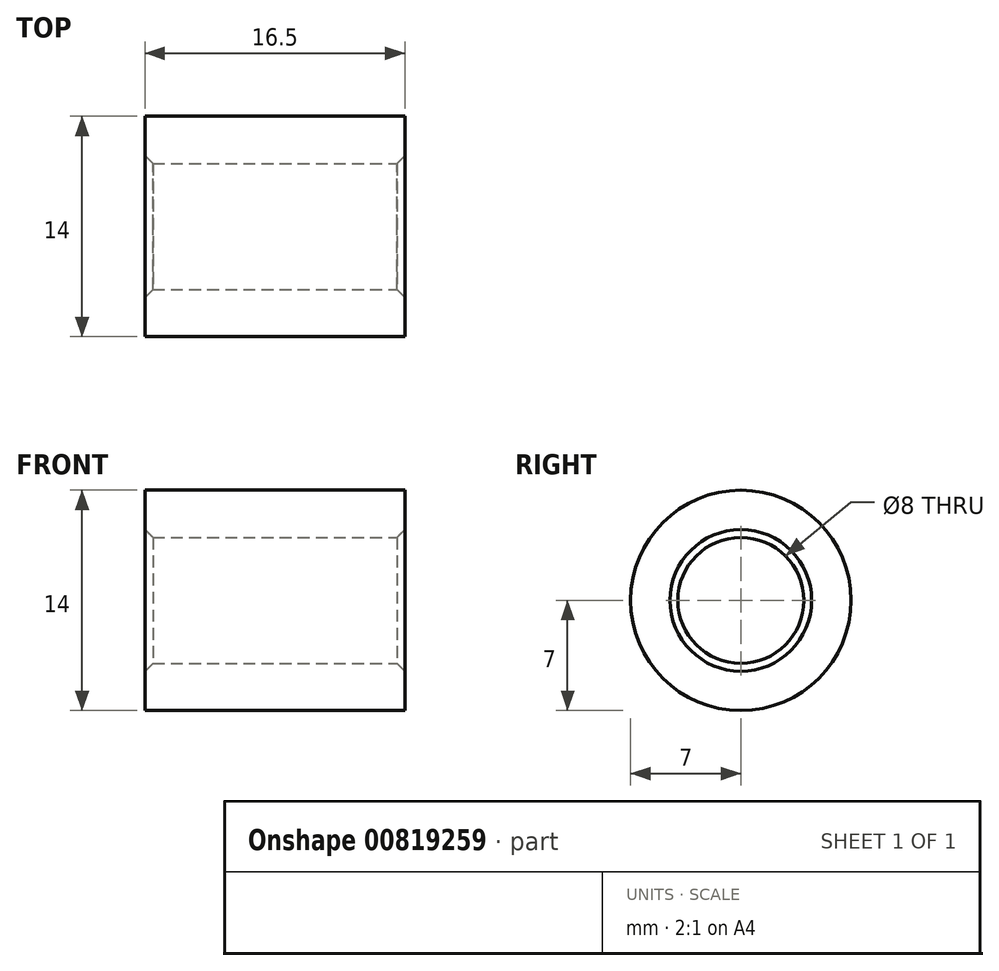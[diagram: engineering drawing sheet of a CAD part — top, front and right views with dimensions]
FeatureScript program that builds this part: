
annotation { "Feature Type Name" : "Feature", "Feature Type Description" : "" }
export const myFeature = defineFeature(function(context is Context, id is Id, definition is map)
    precondition{}
    {
        {
            var Q0;
            Q0=qCreatedBy(makeId("Front.planeOp"),FACE);
            var sketch = newSketch(context, id + "F0", { "sketchPlane" : qUnion([Q0])});
            skLineSegment(sketch, "E0.bottom", {"start": v(-8.25, 7) * mm, "end": v(8.25, 7) * mm});
            skLineSegment(sketch, "E0.top", {"start": v(-8.25, 4) * mm, "end": v(8.25, 4) * mm});
            skLineSegment(sketch, "E0.left", {"start": v(-8.25, 7) * mm, "end": v(-8.25, 4) * mm});
            skLineSegment(sketch, "E0.right", {"start": v(8.25, 7) * mm, "end": v(8.25, 4) * mm});
            skLineSegment(sketch, "E1", {"start": v(24.88, 0) * mm, "end": v(-49.87, 0) * mm, "construction": true});
            skSolve(sketch);
        }
        {
            var Q0;
            Q0=makeQuery(id+"F0.imprint","IMPRINT",FACE,{"disambiguationData":[TD([[makeQuery(id+"F0.imprint","IMPRINT",EDGE,{"derivedFrom":sQuery(id+"F0.wireOp",EDGE,"E0.bottom")}),-1.0]])]});
            var Q1;
            Q1=sQuery(id+"F0.wireOp",EDGE,"E1");
            revolve(context, id + "F1", {"surfaceOperationType" : NewSurfaceOperationType.NEW, "entities" : qUnion([Q0]), "axis" : qUnion([Q1]), "revolveType" : RevolveType.FULL});
        }
        {
            var Q0;
            Q0=makeQuery(id+"F1.opRevolve","SWEPT_EDGE",EDGE,{"disambiguationData":[OSD([sQuery(id+"F0.wireOp",EDGE,"E0.top"),sQuery(id+"F0.wireOp",EDGE,"E0.left")])]});
            var Q1;
            Q1=makeQuery(id+"F1.opRevolve","SWEPT_EDGE",EDGE,{"disambiguationData":[OSD([sQuery(id+"F0.wireOp",EDGE,"E0.top"),sQuery(id+"F0.wireOp",EDGE,"E0.right")])]});
            chamfer(context, id + "F2", {"entities" : qUnion([Q0, Q1]), "chamferType" : ChamferType.OFFSET_ANGLE, "width" : 0.5 * mm, "oppositeDirection" : false, "angle" : 45 * degree, "tangentPropagation" : true});
        }
    });
